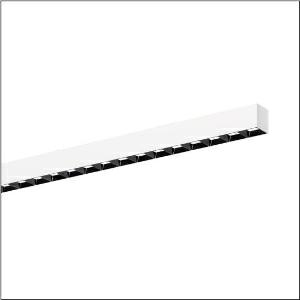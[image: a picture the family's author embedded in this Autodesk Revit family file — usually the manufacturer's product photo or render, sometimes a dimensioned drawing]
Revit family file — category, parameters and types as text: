
# Revit family: silica_r__21_51mx21da34wb_4769
name_source: partatom
category: Lighting Fixtures
units: mm (PartAtom-declared; Revit-internal decimal feet)

## family parameters
Cut with Voids When Loaded = No
Host = Face
Light Source = No
Part Type = Normal
Room Calculation Point = No
Round Connector Dimension = Use Diameter
Shared = No

## types (1)
- --- (1 x LED, 4320 lm, 27.4 W, 3000K)
    Apparent Load = 27 VA
    CIE Flux Codes = 87 99 100 100 100
    Color Rendering = 80
    Color Temperature = 3000K
    Default Elevation = 1800 mm
    Description = Silica® 21, office luminaire, primary light control with darklight reflector, of PMMA, black, CAT 2 (L<= 3000cd/m²), light emission: direct distribution, primary light characteristic: symmetric, installation type: surface-mounted, LED, rated luminous flux: 4.320lm, luminous efficacy: 158lm/W, light colour: 830, colour temperature: 3000K, with terminal, 3+2-pole, max. 2.5mm², mains connection: 220..240V, AC, 50/60Hz, rated input power: 27.4W, luminaire housing, of aluminium, traffic white (RAL 9016), length: 1.204mm, width: 53mm, height: 53mm, protection rating (complete): IP20, insulation class (complete): insulation class I (protective earthing), certification: CE, permissible operating ambient temperature: 0..+35°C, standard: EN 50419, packaging unit: 1 piece
    Height = 0 mm  [stored 0 ft]
    Lamp = 1 x LED
    Lamp Light Flux = 4320 lm
    Lamp Power = 27.4 W
    Lamp count = 1
    Length = 1204 mm
    Luminous efficacy = 158 lm/W
    Manufacturer = Siteco
    ModVariant = No
    Model = 51MX21DA34WB
    Mounting Place = Ceiling
    Mounting Type = Recessed
    Number of Poles = 1
    OnlyDefault = Yes
    Power Factor = 1
    Product Name = Silica® 21
    Product group = office luminaire | ceiling recessed
    ProductGroupID = 401
    Protection Class = Protection class I
    Protection Degree = IP 20
    RLX_Detail_Level = 1
    RLX_Emergency_Light_Flux = 0 lm
    RLX_Emergency_Type = 0
    RLX_Emergency_Type_DB = No
    RlxData = <blob elided: 40893 chars, md5=56e2ad85>
    Socket = socket
    Standby Power = 0 W
    System Light Flux = 4320 lm
    System Power = 27 W
    Type Comments = factory setting: luminous flux: 100 % | dim-lin: 254 | 393 mA
    Type Image = l_1313592.jpg
    URL = http://relux.com
    VarID = @adj_073105
    Voltage = 0 V
    Weight = 0.00 kg
    Width = 53 mm

note: [stored X ft] marks values corroborated as IEEE doubles in the binary element streams (Revit-internal decimal feet)

## geometry (parser evidence)
native form markers: Blend x4, Sweep x10
no freeform markers — native parametric forms only
